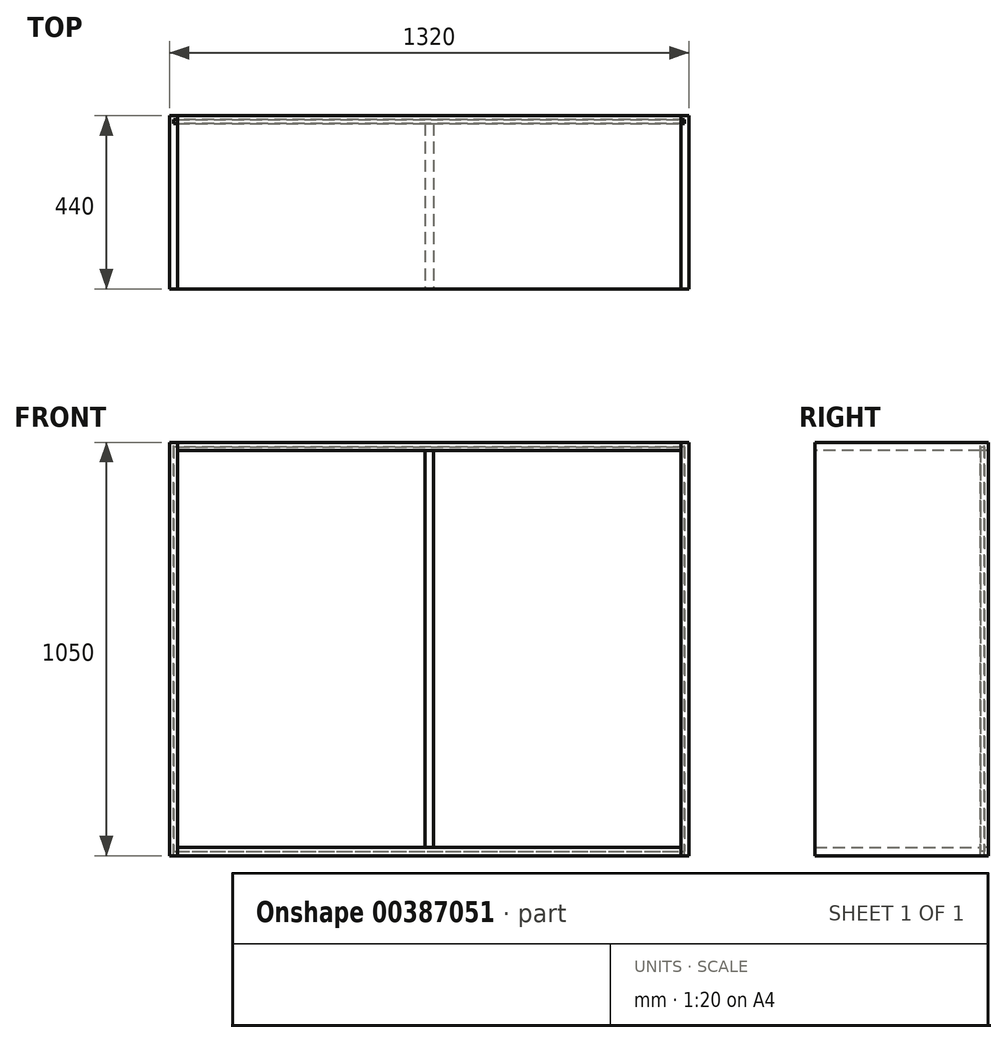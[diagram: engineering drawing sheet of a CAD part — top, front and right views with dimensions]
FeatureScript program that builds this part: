
annotation { "Feature Type Name" : "Feature", "Feature Type Description" : "" }
export const myFeature = defineFeature(function(context is Context, id is Id, definition is map)
    precondition{}
    {
        {
            var Q0;
            Q0=qCreatedBy(makeId("Front.planeOp"),FACE);
            cPlane(context, id + "F0", {"entities" : qUnion([Q0]), "cplaneType" : CPlaneType.OFFSET, "offset" : 440 * mm, "oppositeDirection" : true, "width" : 150 * mm, "height" : 150 * mm});
        }
        {
            var Q0;
            Q0=qCreatedBy(makeId("Right.planeOp"),FACE);
            cPlane(context, id + "F1", {"entities" : qUnion([Q0]), "cplaneType" : CPlaneType.OFFSET, "offset" : 1320 / 2 * mm, "oppositeDirection" : true, "width" : 150 * mm, "height" : 150 * mm});
        }
        {
            var Q0;
            Q0=qCreatedBy(makeId("Top.planeOp"),FACE);
            cPlane(context, id + "F2", {"entities" : qUnion([Q0]), "cplaneType" : CPlaneType.OFFSET, "offset" : 1050 * mm, "oppositeDirection" : true, "width" : 150 * mm, "height" : 150 * mm});
        }
        {
            var Q0;
            Q0=qCreatedBy(makeId("Top.planeOp"),FACE);
            var sketch = newSketch(context, id + "F3", { "sketchPlane" : qUnion([Q0])});
            skLineSegment(sketch, "E0.bottom", {"start": v(-660, 440) * mm, "end": v(-639, 440) * mm});
            skLineSegment(sketch, "E0.top", {"start": v(-660, 0) * mm, "end": v(-639, 0) * mm});
            skLineSegment(sketch, "E0.left", {"start": v(-660, 440) * mm, "end": v(-660, 0) * mm});
            skLineSegment(sketch, "E0.right", {"start": v(-639, 440) * mm, "end": v(-639, 430) * mm});
            skLineSegment(sketch, "E1.bottom", {"start": v(-649, 430) * mm, "end": v(-639, 430) * mm});
            skLineSegment(sketch, "E1.top", {"start": v(-649, 420) * mm, "end": v(-639, 420) * mm});
            skLineSegment(sketch, "E1.left", {"start": v(-649, 430) * mm, "end": v(-649, 420) * mm});
            skLineSegment(sketch, "E2.trimOffspring", {"start": v(-639, 420) * mm, "end": v(-639, 0) * mm});
            skSolve(sketch);
        }
        {
            var Q0;
            Q0=makeQuery(id+"F3.imprint","IMPRINT",FACE,{"disambiguationData":[TD([[makeQuery(id+"F3.imprint","IMPRINT",EDGE,{"derivedFrom":sQuery(id+"F3.wireOp",EDGE,"E0.bottom")}),-1.0]])]});
            var Q1;
            Q1=qCreatedBy(id+"F2.planeOp",FACE);
            extrude(context, id + "F4", {"entities" : qUnion([Q0]), "endBound" : BoundingType.UP_TO_SURFACE, "oppositeDirection" : true, "endBoundEntityFace" : qUnion([Q1]), "depth" : 25 * mm});
        }
        {
            var Q0;
            Q0=makeQuery(id+"F4.opExtrude","SWEPT_BODY",BODY,{"disambiguationData":[OSD([sQuery(id+"F3.wireOp",EDGE,"E0.bottom"),sQuery(id+"F3.wireOp",EDGE,"E0.top"),sQuery(id+"F3.wireOp",EDGE,"E0.left"),sQuery(id+"F3.wireOp",EDGE,"E0.right"),sQuery(id+"F3.wireOp",EDGE,"E1.bottom"),sQuery(id+"F3.wireOp",EDGE,"E1.top"),sQuery(id+"F3.wireOp",EDGE,"E1.left"),sQuery(id+"F3.wireOp",EDGE,"E2.trimOffspring")])]});
            var Q1;
            Q1=qCreatedBy(makeId("Right.planeOp"),FACE);
            mirror(context, id + "F5", {"entities" : qUnion([Q0]), "mirrorPlane" : qUnion([Q1])});
        }
        {
            var Q0;
            Q0=qCreatedBy(makeId("Top.planeOp"),FACE);
            var sketch = newSketch(context, id + "F6", { "sketchPlane" : qUnion([Q0])});
            skLineSegment(sketch, "E3.bottom", {"start": v(-639, 440) * mm, "end": v(639, 440) * mm});
            skLineSegment(sketch, "E3.top", {"start": v(-639, 0) * mm, "end": v(639, 0) * mm});
            skLineSegment(sketch, "E3.left", {"start": v(-639, 440) * mm, "end": v(-639, 0) * mm});
            skLineSegment(sketch, "E3.right", {"start": v(639, 440) * mm, "end": v(639, 0) * mm});
            skSolve(sketch);
        }
        {
            var Q0;
            Q0=makeQuery(id+"F6.imprint","IMPRINT",FACE,{"disambiguationData":[TD([[makeQuery(id+"F6.imprint","IMPRINT",EDGE,{"derivedFrom":sQuery(id+"F6.wireOp",EDGE,"E3.bottom")}),-1.0]])]});
            extrude(context, id + "F7", {"entities" : qUnion([Q0]), "oppositeDirection" : true, "depth" : 21 * mm});
        }
        {
            var Q0;
            Q0=makeQuery(id+"F7.opExtrude","SWEPT_FACE",FACE,{"disambiguationData":[OSD([sQuery(id+"F6.wireOp",EDGE,"E3.right")])]});
            var sketch = newSketch(context, id + "F8", { "sketchPlane" : qUnion([Q0])});
            skLineSegment(sketch, "E4.bottom", {"start": v(420, -11) * mm, "end": v(430, -11) * mm});
            skLineSegment(sketch, "E4.top", {"start": v(420, -21) * mm, "end": v(430, -21) * mm});
            skLineSegment(sketch, "E4.left", {"start": v(420, -11) * mm, "end": v(420, -21) * mm});
            skLineSegment(sketch, "E4.right", {"start": v(430, -11) * mm, "end": v(430, -21) * mm});
            skSolve(sketch);
        }
        {
            var Q0;
            Q0 = qSketchRegion(id + "F8", true);
            var Q1;
            Q1=makeQuery(id+"F7.opExtrude","SWEPT_BODY",BODY,{"disambiguationData":[OSD([sQuery(id+"F6.wireOp",EDGE,"E3.bottom"),sQuery(id+"F6.wireOp",EDGE,"E3.top"),sQuery(id+"F6.wireOp",EDGE,"E3.left"),sQuery(id+"F6.wireOp",EDGE,"E3.right")])]});
            extrude(context, id + "F9", {"entities" : qUnion([Q0]), "operationType" : NewBodyOperationType.REMOVE, "endBound" : BoundingType.UP_TO_BODY, "oppositeDirection" : true, "endBoundEntityBody" : qUnion([Q1]), "depth" : 25 * mm});
        }
        {
            var Q0;
            Q0=qCreatedBy(makeId("Top.planeOp"),FACE);
            cPlane(context, id + "F10", {"entities" : qUnion([Q0]), "cplaneType" : CPlaneType.OFFSET, "offset" : (1050 / 2) * mm, "oppositeDirection" : true, "width" : 150 * mm, "height" : 150 * mm});
        }
        {
            var Q0;
            Q0=makeQuery(id+"F7.opExtrude","SWEPT_BODY",BODY,{"disambiguationData":[OSD([sQuery(id+"F6.wireOp",EDGE,"E3.bottom"),sQuery(id+"F6.wireOp",EDGE,"E3.top"),sQuery(id+"F6.wireOp",EDGE,"E3.left"),sQuery(id+"F6.wireOp",EDGE,"E3.right")])]});
            var Q1;
            Q1=qCreatedBy(id+"F10.planeOp",FACE);
            mirror(context, id + "F11", {"entities" : qUnion([Q0]), "mirrorPlane" : qUnion([Q1])});
        }
        {
            var Q0;
            Q0=qCreatedBy(id+"F10.planeOp",FACE);
            var sketch = newSketch(context, id + "F12", { "sketchPlane" : qUnion([Q0])});
            skLineSegment(sketch, "E5.bottom", {"start": v(-10.5, 420) * mm, "end": v(10.5, 420) * mm});
            skLineSegment(sketch, "E5.top", {"start": v(-10.5, 0) * mm, "end": v(10.5, 0) * mm});
            skLineSegment(sketch, "E5.left", {"start": v(-10.5, 420) * mm, "end": v(-10.5, 0) * mm});
            skLineSegment(sketch, "E5.right", {"start": v(10.5, 420) * mm, "end": v(10.5, 0) * mm});
            skSolve(sketch);
        }
        {
            var Q0;
            Q0=makeQuery(id+"F12.imprint","IMPRINT",FACE,{"disambiguationData":[TD([[makeQuery(id+"F12.imprint","IMPRINT",EDGE,{"derivedFrom":sQuery(id+"F12.wireOp",EDGE,"E5.bottom")}),-1.0]])]});
            var Q1;
            Q1=makeQuery(id+"F7.opExtrude","SWEPT_BODY",BODY,{"disambiguationData":[OSD([sQuery(id+"F6.wireOp",EDGE,"E3.bottom"),sQuery(id+"F6.wireOp",EDGE,"E3.top"),sQuery(id+"F6.wireOp",EDGE,"E3.left"),sQuery(id+"F6.wireOp",EDGE,"E3.right")])]});
            var Q2;
            Q2=makeQuery(id+"F11.opPattern","COPY",BODY,{"derivedFrom":makeQuery(id+"F7.opExtrude","SWEPT_BODY",BODY,{"disambiguationData":[OSD([sQuery(id+"F6.wireOp",EDGE,"E3.bottom"),sQuery(id+"F6.wireOp",EDGE,"E3.top"),sQuery(id+"F6.wireOp",EDGE,"E3.left"),sQuery(id+"F6.wireOp",EDGE,"E3.right")])]}),"instanceName":"1"});
            extrude(context, id + "F13", {"entities" : qUnion([Q0]), "endBound" : BoundingType.UP_TO_BODY, "endBoundEntityBody" : qUnion([Q1]), "depth" : 25 * mm, "hasSecondDirection" : true, "secondDirectionBound" : SecondDirectionBoundingType.UP_TO_BODY, "secondDirectionOppositeDirection" : true, "secondDirectionBoundEntityBody" : qUnion([Q2]), "secondDirectionDepth" : 25 * mm});
        }
        {
            var Q0;
            Q0=qCreatedBy(id+"F10.planeOp",FACE);
            var sketch = newSketch(context, id + "F14", { "sketchPlane" : qUnion([Q0])});
            skLineSegment(sketch, "E6.bottom", {"start": v(-649, 430) * mm, "end": v(649, 430) * mm});
            skLineSegment(sketch, "E6.top", {"start": v(-649, 420) * mm, "end": v(649, 420) * mm});
            skLineSegment(sketch, "E6.left", {"start": v(-649, 430) * mm, "end": v(-649, 420) * mm});
            skLineSegment(sketch, "E6.right", {"start": v(649, 430) * mm, "end": v(649, 420) * mm});
            skSolve(sketch);
        }
        {
            var Q0;
            Q0=makeQuery(id+"F14.imprint","IMPRINT",FACE,{"disambiguationData":[TD([[makeQuery(id+"F14.imprint","IMPRINT",EDGE,{"derivedFrom":sQuery(id+"F14.wireOp",EDGE,"E6.bottom")}),-1.0]])]});
            var Q1;
            Q1=makeQuery(id+"F9.boolean.opBoolean","COPY",FACE,{"derivedFrom":makeQuery(id+"F9.opExtrude","SWEPT_FACE",FACE,{"disambiguationData":[OSD([sQuery(id+"F8.wireOp",EDGE,"E4.bottom")])]})});
            var Q2;
            Q2=makeQuery(id+"F11.opPattern","COPY",FACE,{"derivedFrom":makeQuery(id+"F9.boolean.opBoolean","COPY",FACE,{"derivedFrom":makeQuery(id+"F9.opExtrude","SWEPT_FACE",FACE,{"disambiguationData":[OSD([sQuery(id+"F8.wireOp",EDGE,"E4.bottom")])]})}),"instanceName":"1"});
            extrude(context, id + "F15", {"entities" : qUnion([Q0]), "endBound" : BoundingType.UP_TO_SURFACE, "endBoundEntityFace" : qUnion([Q1]), "depth" : 25 * mm, "hasSecondDirection" : true, "secondDirectionBound" : SecondDirectionBoundingType.UP_TO_SURFACE, "secondDirectionOppositeDirection" : true, "secondDirectionBoundEntityFace" : qUnion([Q2]), "secondDirectionDepth" : 25 * mm});
        }
    });
